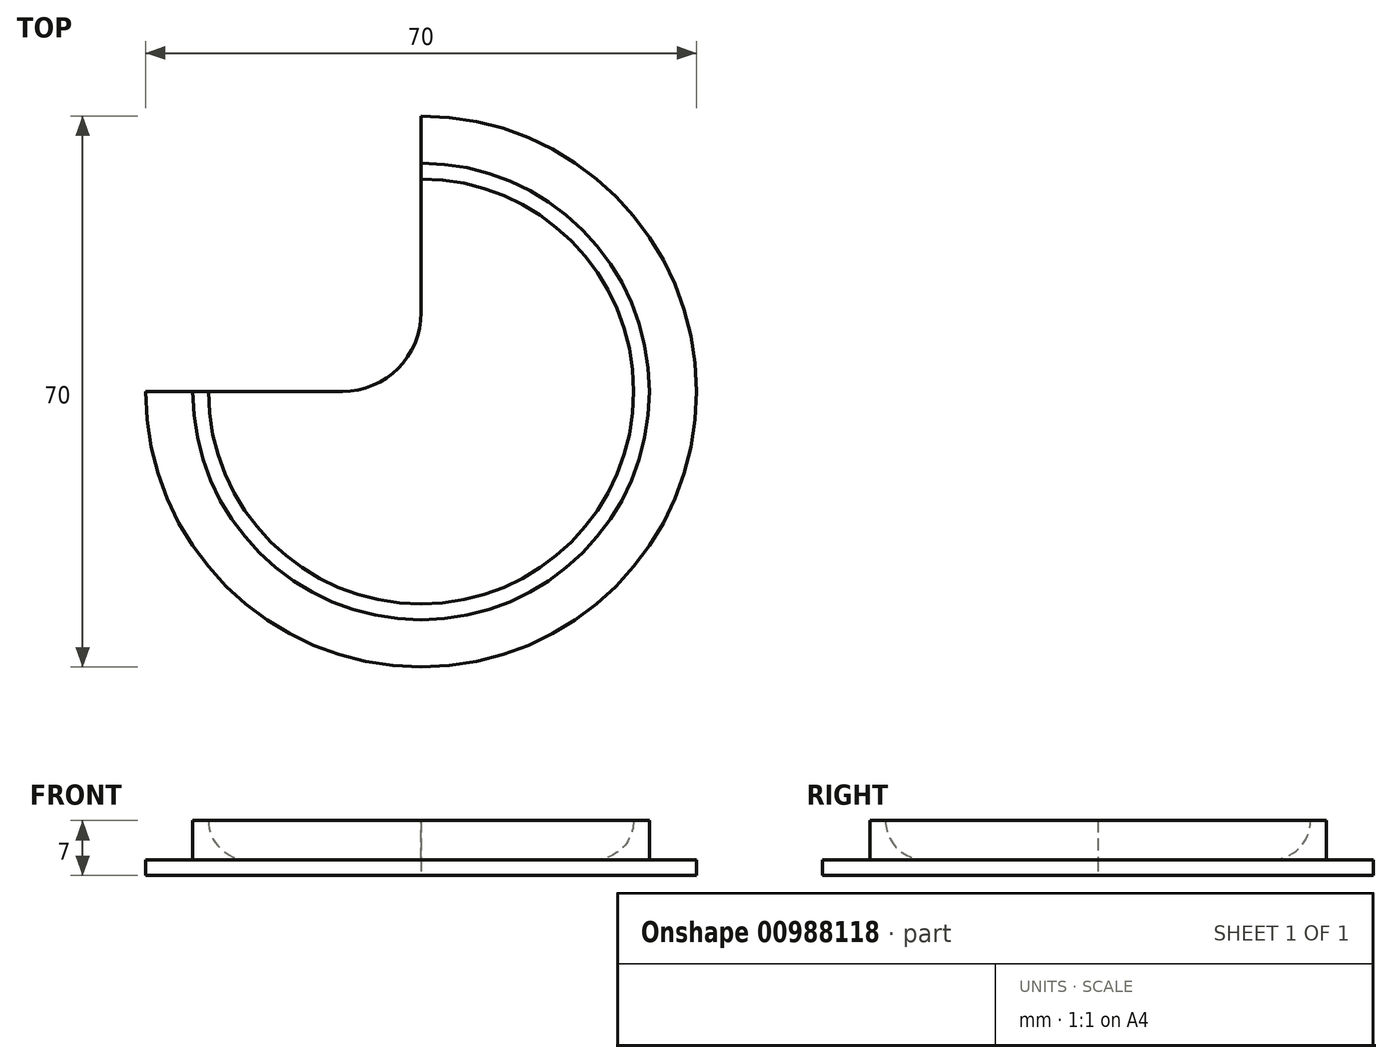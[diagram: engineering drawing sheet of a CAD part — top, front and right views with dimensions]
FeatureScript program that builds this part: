
annotation { "Feature Type Name" : "Feature", "Feature Type Description" : "" }
export const myFeature = defineFeature(function(context is Context, id is Id, definition is map)
    precondition{}
    {
        {
            var Q0;
            Q0=qCreatedBy(makeId("Top.planeOp"),FACE);
            var sketch = newSketch(context, id + "F0", { "sketchPlane" : qUnion([Q0])});
            skCircle(sketch, "E0", {"center": v(0, 0) * mm, "radius": 35 * mm});
            skSolve(sketch);
        }
        {
            var Q0;
            Q0 = qSketchRegion(id + "F0", true);
            extrude(context, id + "F1", {"entities" : qUnion([Q0]), "depth" : 2 * mm, "offsetDistance" : 25 * mm});
        }
        {
            var Q0;
            Q0=makeQuery(id+"F1.opExtrude","CAP_FACE",FACE,{"disambiguationData":[OSD([sQuery(id+"F0.wireOp",EDGE,"E0")])],"isStart":false});
            var sketch = newSketch(context, id + "F2", { "sketchPlane" : qUnion([Q0])});
            skCircle(sketch, "E1", {"center": v(0, 0) * mm, "radius": 29 * mm});
            skSolve(sketch);
        }
        {
            var Q0;
            Q0 = qSketchRegion(id + "F2", true);
            extrude(context, id + "F3", {"entities" : qUnion([Q0]), "operationType" : NewBodyOperationType.ADD, "depth" : 5 * mm, "offsetDistance" : 25 * mm});
        }
        {
            var Q0;
            Q0=makeQuery(id+"F3.opExtrude","CAP_FACE",FACE,{"disambiguationData":[OSD([sQuery(id+"F2.wireOp",EDGE,"E1")])],"isStart":false});
            var sketch = newSketch(context, id + "F4", { "sketchPlane" : qUnion([Q0])});
            skCircle(sketch, "E2", {"center": v(0, 0) * mm, "radius": 27 * mm});
            skSolve(sketch);
        }
        {
            var Q0;
            Q0 = qSketchRegion(id + "F4", true);
            var Q1;
            Q1=makeQuery(id+"F1.opExtrude","CAP_FACE",FACE,{"disambiguationData":[OSD([sQuery(id+"F0.wireOp",EDGE,"E0")])],"isStart":false});
            extrude(context, id + "F5", {"entities" : qUnion([Q0]), "operationType" : NewBodyOperationType.REMOVE, "endBound" : BoundingType.UP_TO_SURFACE, "oppositeDirection" : true, "depth" : 25 * mm, "endBoundEntityFace" : qUnion([Q1]), "offsetDistance" : 25 * mm});
        }
        {
            var Q0;
            Q0=makeQuery(id+"F5.boolean.opBoolean","COPY",FACE,{"derivedFrom":makeQuery(id+"F5.opExtrude","CAP_FACE",FACE,{"disambiguationData":[OSD([sQuery(id+"F4.wireOp",EDGE,"E2")])],"isStart":false})});
            var sketch = newSketch(context, id + "F6", { "sketchPlane" : qUnion([Q0])});
            skLineSegment(sketch, "E3", {"start": v(0, 0) * mm, "end": v(0, 45.14) * mm});
            skLineSegment(sketch, "E4", {"start": v(0, 45.14) * mm, "end": v(-45.18, 45.14) * mm});
            skLineSegment(sketch, "E5", {"start": v(-45.18, 45.14) * mm, "end": v(-45.18, 0) * mm});
            skLineSegment(sketch, "E6", {"start": v(-45.18, 0) * mm, "end": v(0, 0) * mm});
            skSolve(sketch);
        }
        {
            var Q0;
            Q0 = qSketchRegion(id + "F6", true);
            extrude(context, id + "F7", {"entities" : qUnion([Q0]), "operationType" : NewBodyOperationType.REMOVE, "endBound" : BoundingType.THROUGH_ALL, "oppositeDirection" : true, "depth" : 25 * mm, "offsetDistance" : 25 * mm, "hasSecondDirection" : true, "secondDirectionBound" : SecondDirectionBoundingType.THROUGH_ALL, "secondDirectionOppositeDirection" : false, "secondDirectionDepth" : 25 * mm});
        }
        {
            var Q0;
            Q0=makeQuery(id+"F5.boolean.opBoolean","COPY",EDGE,{"derivedFrom":makeQuery(id+"F5.opExtrude","CAP_EDGE",EDGE,{"disambiguationData":[OSD([sQuery(id+"F4.wireOp",EDGE,"E2")])],"isStart":false})});
            fillet(context, id + "F8", {"entities" : qUnion([Q0]), "tangentPropagation" : true, "radius" : 5 * mm, "defaultsChanged" : true, "vertexSettings" : [], "allowEdgeOverflow" : false});
        }
        {
            var Q0;
            Q0=makeQuery(id+"F7.boolean.opBoolean","COPY",EDGE,{"derivedFrom":makeQuery(id+"F7.opExtrude","SWEPT_EDGE",EDGE,{"disambiguationData":[OSD([sQuery(id+"F6.wireOp",EDGE,"E3"),sQuery(id+"F6.wireOp",EDGE,"E6")])]})});
            fillet(context, id + "F9", {"entities" : qUnion([Q0]), "tangentPropagation" : true, "radius" : 10 * mm, "defaultsChanged" : true, "vertexSettings" : [], "allowEdgeOverflow" : false});
        }
    });
